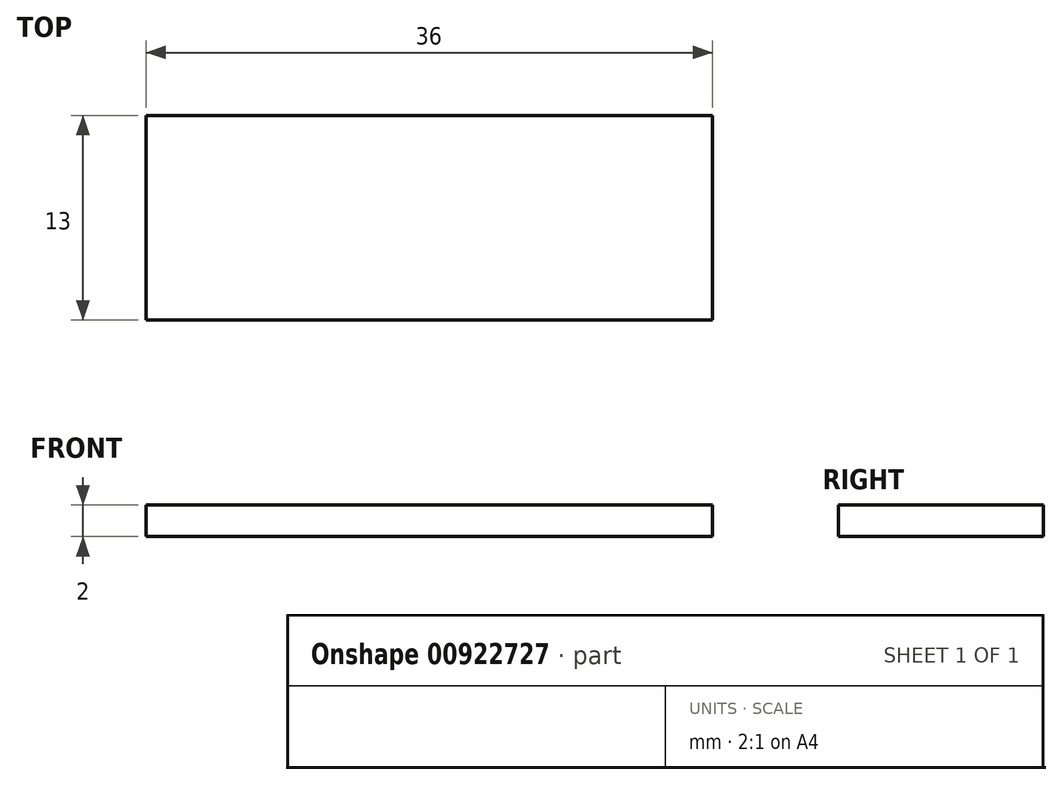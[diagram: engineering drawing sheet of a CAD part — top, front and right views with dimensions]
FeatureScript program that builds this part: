
annotation { "Feature Type Name" : "Feature", "Feature Type Description" : "" }
export const myFeature = defineFeature(function(context is Context, id is Id, definition is map)
    precondition{}
    {
        {
            var Q0;
            Q0=qCreatedBy(makeId("Top.planeOp"),FACE);
            var sketch = newSketch(context, id + "F0", { "sketchPlane" : qUnion([Q0])});
            skLineSegment(sketch, "E0.bottom", {"start": v(18, -6.5) * mm, "end": v(-18, -6.5) * mm});
            skLineSegment(sketch, "E0.top", {"start": v(18, 6.5) * mm, "end": v(-18, 6.5) * mm});
            skLineSegment(sketch, "E0.left", {"start": v(18, -6.5) * mm, "end": v(18, 6.5) * mm});
            skLineSegment(sketch, "E0.right", {"start": v(-18, -6.5) * mm, "end": v(-18, 6.5) * mm});
            skPoint(sketch, "E0.middle", {"position": v(0, 0) * mm});
            skSolve(sketch);
        }
        {
            var Q0;
            Q0 = qSketchRegion(id + "F0", true);
            extrude(context, id + "F1", {"entities" : qUnion([Q0]), "endBound" : BoundingType.SYMMETRIC, "depth" : 2 * mm, "offsetDistance" : 25 * mm});
        }
    });
